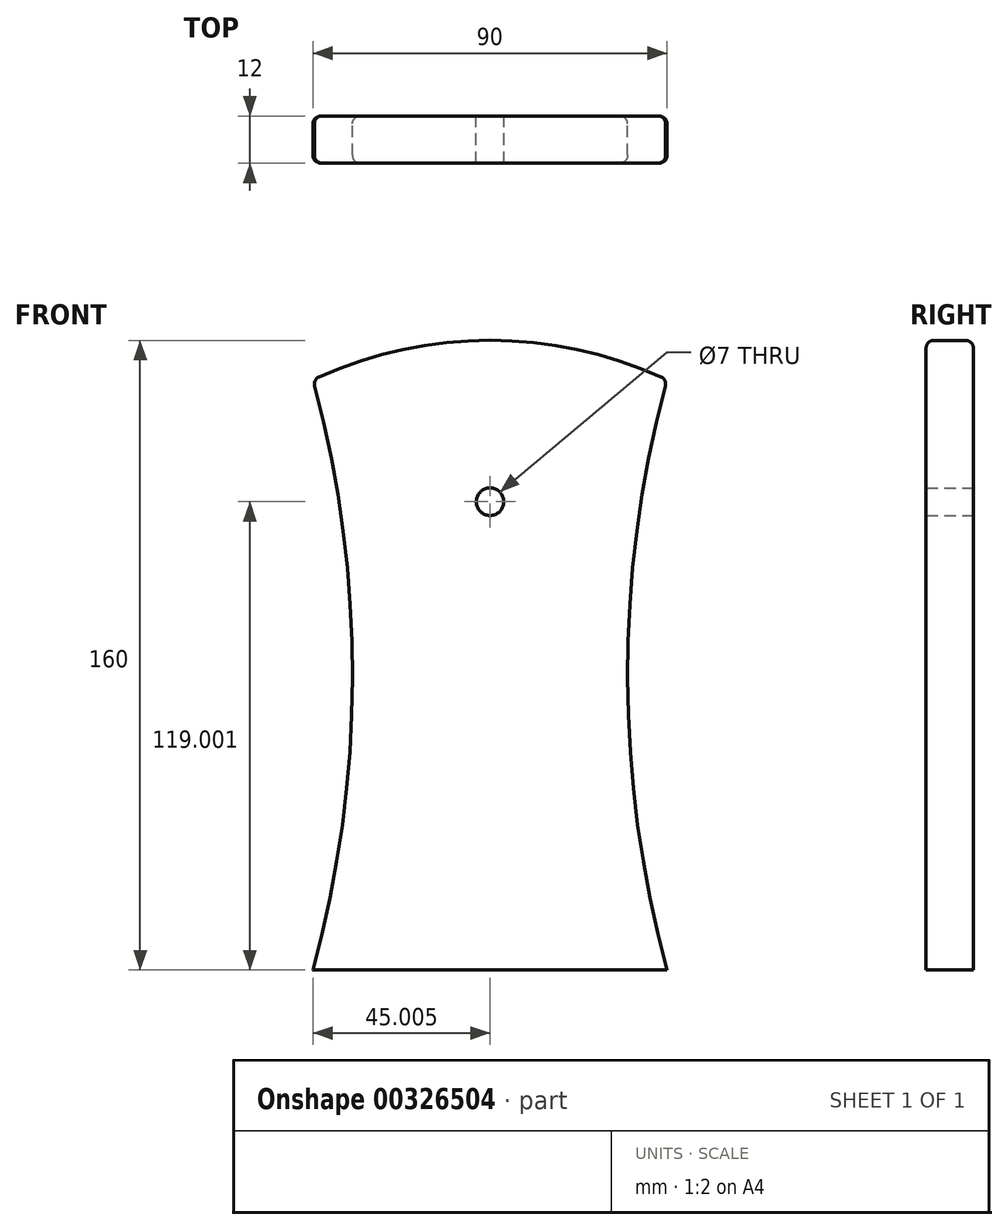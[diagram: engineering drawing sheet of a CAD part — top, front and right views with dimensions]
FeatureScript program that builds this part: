
annotation { "Feature Type Name" : "Feature", "Feature Type Description" : "" }
export const myFeature = defineFeature(function(context is Context, id is Id, definition is map)
    precondition{}
    {
        {
            var Q0;
            Q0=qCreatedBy(makeId("Front.planeOp"),FACE);
            var sketch = newSketch(context, id + "F0", { "sketchPlane" : qUnion([Q0])});
            skLineSegment(sketch, "E0", {"start": v(-95.08, -59.83) * mm, "end": v(-5.08, -59.83) * mm});
            skLineSegment(sketch, "E1", {"start": v(-95.08, 20.17) * mm, "end": v(-85.08, 20.17) * mm, "construction": true});
            skLineSegment(sketch, "E2", {"start": v(-5.08, 20.17) * mm, "end": v(-15.08, 20.17) * mm, "construction": true});
            skLineSegment(sketch, "E3", {"start": v(-95.08, 90.17) * mm, "end": v(-5.08, 90.17) * mm, "construction": true});
            skPoint(sketch, "E4", {"position": v(-50.08, 100.17) * mm});
            skArc(sketch, "E5", {"start": v(-5.08, 90.17) * mm, "mid": v(-50.08, 100.17) * mm, "end": v(-95.08, 90.17) * mm});
            skArc(sketch, "E6", {"start": v(-95.08, -59.83) * mm, "mid": v(-85.03, 15.17) * mm, "end": v(-95.08, 90.17) * mm});
            skArc(sketch, "E7", {"start": v(-5.08, 90.17) * mm, "mid": v(-15.12, 15.17) * mm, "end": v(-5.08, -59.83) * mm});
            skPoint(sketch, "E8.trimOffspring.end.orphan", {"position": v(-5.08, 100.17) * mm});
            skPoint(sketch, "E9.start.orphan", {"position": v(-95.08, 100.17) * mm});
            skLineSegment(sketch, "E10", {"start": v(-50.08, -59.83) * mm, "end": v(-50.08, 59.17) * mm, "construction": true});
            skCircle(sketch, "E11", {"center": v(-50.08, 59.17) * mm, "radius": 3.5 * mm});
            skSolve(sketch);
        }
        {
            var Q0;
            Q0=makeQuery(id+"F0.imprint","IMPRINT",FACE,{"disambiguationData":[TD([[makeQuery(id+"F0.imprint","IMPRINT",EDGE,{"derivedFrom":sQuery(id+"F0.wireOp",EDGE,"E0")}),1.0]])]});
            extrude(context, id + "F1", {"entities" : qUnion([Q0]), "depth" : 12 * mm});
        }
        {
            var Q0;
            Q0=makeQuery(id+"F1.opExtrude","CAP_EDGE",EDGE,{"disambiguationData":[OSD([sQuery(id+"F0.wireOp",EDGE,"E5")])],"isStart":false});
            var Q1;
            Q1=makeQuery(id+"F1.opExtrude","CAP_EDGE",EDGE,{"disambiguationData":[OSD([sQuery(id+"F0.wireOp",EDGE,"E5")])],"isStart":true});
            var Q2;
            Q2=makeQuery(id+"F1.opExtrude","CAP_EDGE",EDGE,{"disambiguationData":[OSD([sQuery(id+"F0.wireOp",EDGE,"E7")])],"isStart":false});
            var Q3;
            Q3=makeQuery(id+"F1.opExtrude","CAP_EDGE",EDGE,{"disambiguationData":[OSD([sQuery(id+"F0.wireOp",EDGE,"E7")])],"isStart":true});
            var Q4;
            Q4=makeQuery(id+"F1.opExtrude","SWEPT_EDGE",EDGE,{"disambiguationData":[OSD([sQuery(id+"F0.wireOp",EDGE,"E5"),sQuery(id+"F0.wireOp",EDGE,"E7")])]});
            var Q5;
            Q5=makeQuery(id+"F1.opExtrude","SWEPT_EDGE",EDGE,{"disambiguationData":[OSD([sQuery(id+"F0.wireOp",EDGE,"E5"),sQuery(id+"F0.wireOp",EDGE,"E6")])]});
            var Q6;
            Q6=makeQuery(id+"F1.opExtrude","CAP_EDGE",EDGE,{"disambiguationData":[OSD([sQuery(id+"F0.wireOp",EDGE,"E6")])],"isStart":true});
            var Q7;
            Q7=makeQuery(id+"F1.opExtrude","CAP_EDGE",EDGE,{"disambiguationData":[OSD([sQuery(id+"F0.wireOp",EDGE,"E6")])],"isStart":false});
            fillet(context, id + "F2", {"entities" : qUnion([Q0, Q1, Q2, Q3, Q4, Q5, Q6, Q7]), "radius" : 2 * mm, "tangentPropagation" : true, "allowEdgeOverflow" : false});
        }
    });
